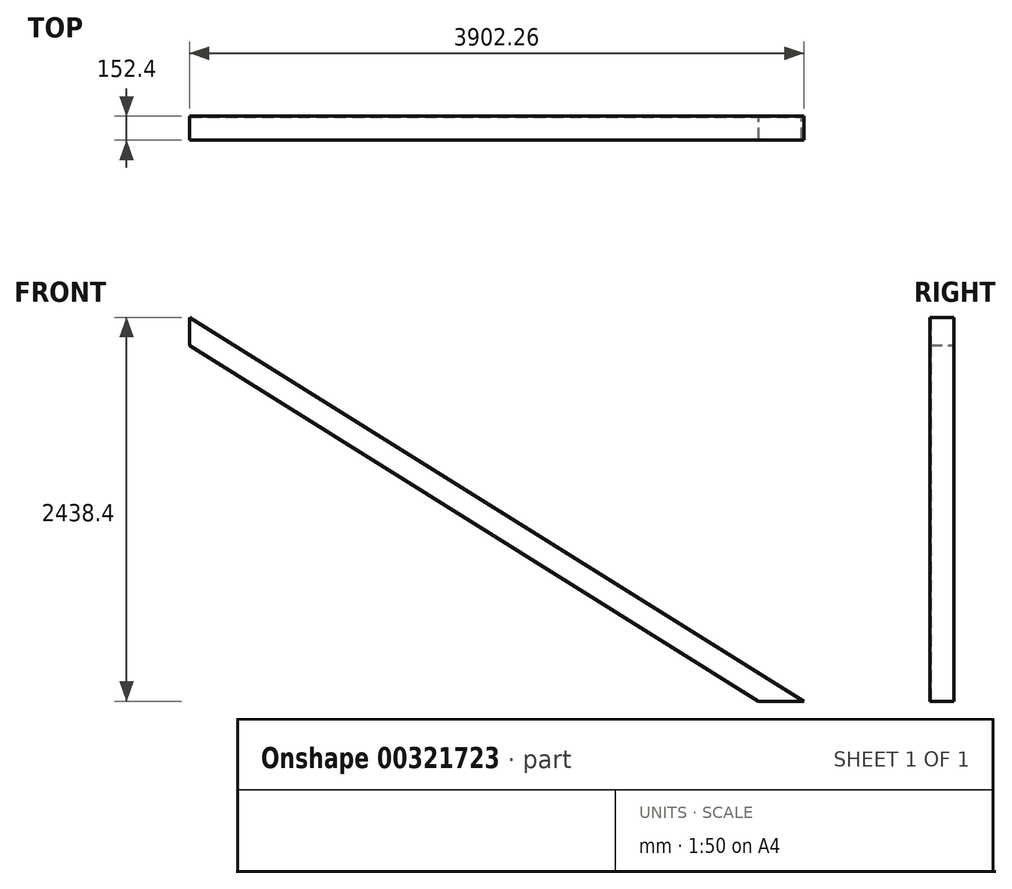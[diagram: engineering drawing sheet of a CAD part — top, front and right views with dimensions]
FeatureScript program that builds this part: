
annotation { "Feature Type Name" : "Feature", "Feature Type Description" : "" }
export const myFeature = defineFeature(function(context is Context, id is Id, definition is map)
    precondition{}
    {
        {
            var Q0;
            Q0=qCreatedBy(makeId("Front.planeOp"),FACE);
            var sketch = newSketch(context, id + "F0", { "sketchPlane" : qUnion([Q0])});
            skLineSegment(sketch, "E0", {"start": v(0, 0) * mm, "end": v(-3902.26, 2438.4) * mm});
            skLineSegment(sketch, "E1", {"start": v(-3902.26, 2258.7) * mm, "end": v(-287.6, 0) * mm});
            skLineSegment(sketch, "E2", {"start": v(-287.6, 0) * mm, "end": v(0, 0) * mm});
            skLineSegment(sketch, "E3", {"start": v(-3902.26, 2438.4) * mm, "end": v(-3902.26, 2258.7) * mm});
            skSolve(sketch);
        }
        {
            var Q0;
            Q0 = qSketchRegion(id + "F0", true);
            extrude(context, id + "F1", {"entities" : qUnion([Q0]), "depth" : 152.4 * mm});
        }
        {
            var Q0;
            Q0=makeQuery(id+"F1.opExtrude","SWEPT_FACE",FACE,{"disambiguationData":[OSD([sQuery(id+"F0.wireOp",EDGE,"E3")])]});
            shell(context, id + "F2", {"entities" : qUnion([Q0]), "thickness" : 4.76 * mm});
        }
    });
